# Revit family: Tub_Spout-American_Standard-Green_Tea-8888_Series
name_source: partatom
category: Plumbing Fixtures
revit_build: Autodesk Revit 2015 (Build: 20140606_1530(x64)
units: mm (PartAtom-declared; Revit-internal decimal feet)

## types (2) — shared parameters
ADA Compliant = Yes
Assembly Code = D2020300
CW Connection = Yes
CWFU = 3
Default Elevation = 25"
Description = Green Tea Diverter Tub Spout
HW Connection = Yes
HWFU = 3
Length = 5 7/8"
Manufacturer = American Standard
NPT Connection Radius = 1/4"
NPT Connection Size = 1/2"
Price = Prices may vary. Please consult Manufacturer Representative for most up-to-date price list.
Product Documentation Link = https://www.americanstandard-us.com
Product Page URL = https://www.americanstandard-us.com
URL = http://www.americanstandard-us.com
Vent Connection = No
WFU = 4
Warranty Information = Limited Lifetime Function and Finish Warranty.
Waste Connection = No

## per-type parameters (varying)
| type | Finish | Material |
| 8888.086.002 | Brass-American Standard-002-Polished Chrome | Brass-American Standard-002-Polished Chrome |
| 8888.086.075 | Metal-American Standard-075-Stainless Steel | Metal-American Standard-075-Stainless Steel |

note: column(s) folded — value = type name in every type: Model

## geometry (parser evidence)
native form markers: Sweep x5
no freeform markers — native parametric forms only
